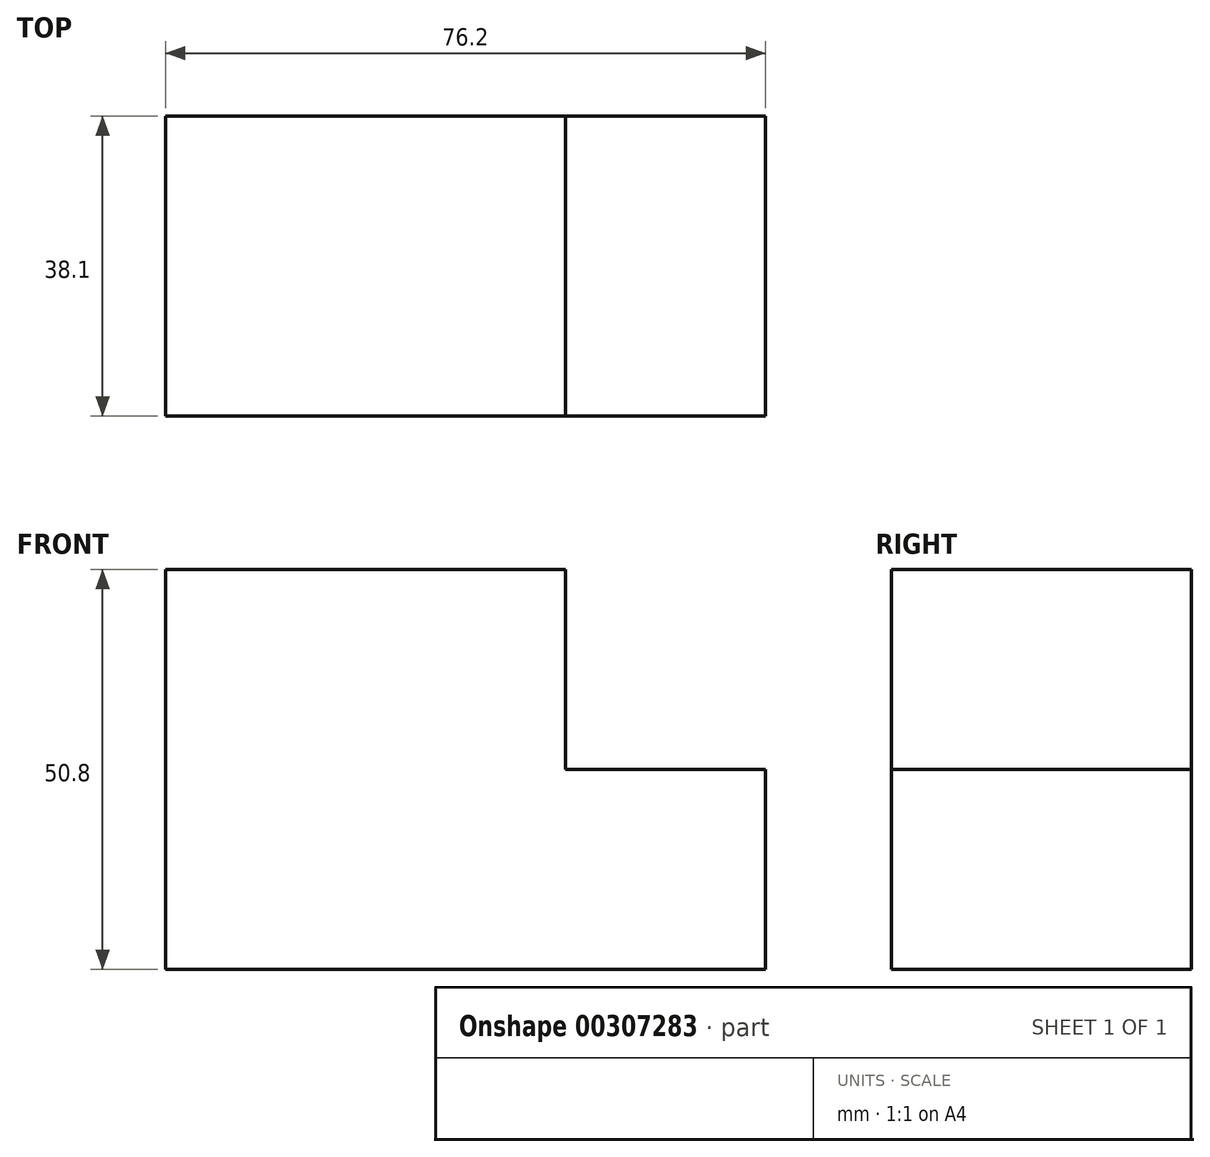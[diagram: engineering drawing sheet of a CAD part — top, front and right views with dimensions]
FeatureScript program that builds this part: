
annotation { "Feature Type Name" : "Feature", "Feature Type Description" : "" }
export const myFeature = defineFeature(function(context is Context, id is Id, definition is map)
    precondition{}
    {
        {
            var Q0;
            Q0=qCreatedBy(makeId("Front.planeOp"),FACE);
            var sketch = newSketch(context, id + "F0", { "sketchPlane" : qUnion([Q0])});
            skLineSegment(sketch, "E0", {"start": v(-41.8, -25.4) * mm, "end": v(-41.8, 25.4) * mm});
            skLineSegment(sketch, "E1", {"start": v(-41.8, 25.4) * mm, "end": v(9, 25.4) * mm});
            skLineSegment(sketch, "E2", {"start": v(9, 25.4) * mm, "end": v(9, 0) * mm});
            skLineSegment(sketch, "E3", {"start": v(9, 0) * mm, "end": v(34.4, 0) * mm});
            skLineSegment(sketch, "E4", {"start": v(34.4, 0) * mm, "end": v(34.4, -25.4) * mm});
            skLineSegment(sketch, "E5", {"start": v(34.4, -25.4) * mm, "end": v(-41.8, -25.4) * mm});
            skSolve(sketch);
        }
        {
            var Q0;
            Q0=makeQuery(id+"F0.imprint","IMPRINT",FACE,{"disambiguationData":[TD([[makeQuery(id+"F0.imprint","IMPRINT",EDGE,{"derivedFrom":sQuery(id+"F0.wireOp",EDGE,"E0")}),-1.0]])]});
            extrude(context, id + "F1", {"entities" : qUnion([Q0]), "depth" : 38.1 * mm});
        }
    });
